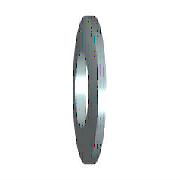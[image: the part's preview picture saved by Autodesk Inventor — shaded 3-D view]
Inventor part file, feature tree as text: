
AUTODESK INVENTOR PART (.ipt)
format: ipt  version: 2025 (Build 290162010, 162A)  size: 130,048 bytes
history: native  units: mm (DEFAULTED — no unit token found)
features: other x2, plane x1, extrude x1, sketch x1
ambient origin geometry x7: Origin, YZ Plane, XY Plane, X Axis, Y Axis, Z Axis, Center Point
bodies: Solid1 (feature_tree)
feature tree (5):
  other  "IDS_BODY"
  other  "Work Axis1"
  plane  "Work Plane1"
  extrude  "Extrusion2"  Depth=2.5mm
  sketch  "Sketch5"  dims[d6=0.0mm d8=2.5mm d10=1.1mm d11=0.6mm d12=0.4mm d13=90.0deg d14=0.0mm d15=0.0mm d17=0.0mm d18=0.0mm d19=2.2mm d20=5.0mm d21=0.6mm d22=0.0mm]
